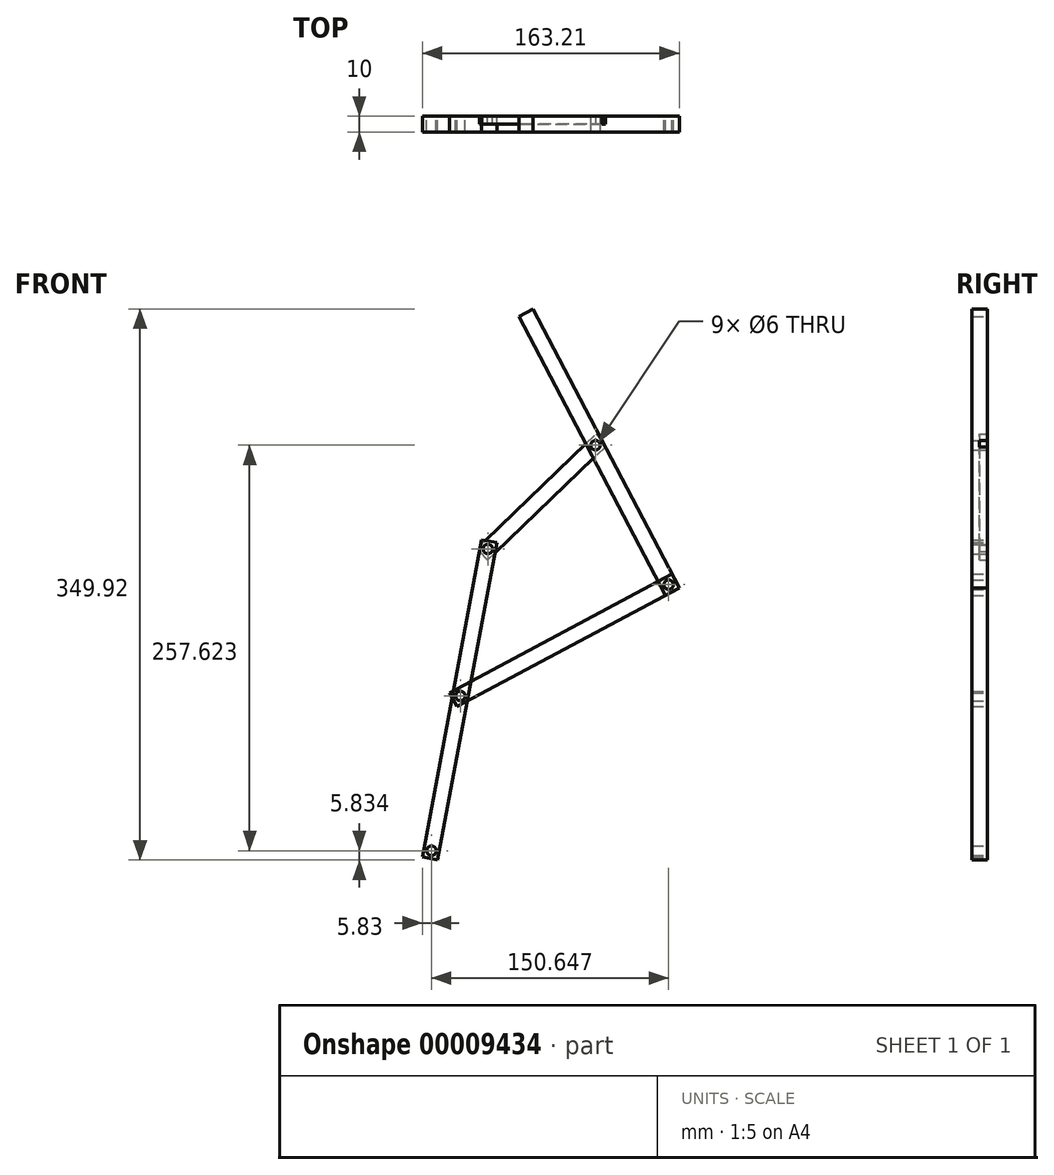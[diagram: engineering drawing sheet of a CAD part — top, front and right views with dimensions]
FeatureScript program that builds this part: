
annotation { "Feature Type Name" : "Feature", "Feature Type Description" : "" }
export const myFeature = defineFeature(function(context is Context, id is Id, definition is map)
    precondition{}
    {
        {
            var Q0;
            Q0=qCreatedBy(makeId("Front.planeOp"),FACE);
            var sketch = newSketch(context, id + "F0", { "sketchPlane" : qUnion([Q0])});
            skLineSegment(sketch, "E0", {"start": v(147.03, 163.63) * mm, "end": v(239.87, -13.52) * mm});
            skLineSegment(sketch, "E1", {"start": v(239.87, -13.52) * mm, "end": v(248.73, -8.87) * mm});
            skLineSegment(sketch, "E2", {"start": v(248.73, -8.87) * mm, "end": v(155.89, 168.27) * mm});
            skLineSegment(sketch, "E3", {"start": v(155.89, 168.27) * mm, "end": v(147.03, 163.63) * mm});
            skCircle(sketch, "E4", {"center": v(241.98, -6.77) * mm, "radius": 3 * mm});
            skCircle(sketch, "E5", {"center": v(195.56, 81.8) * mm, "radius": 3 * mm});
            skLineSegment(sketch, "E6", {"start": v(191.13, 79.49) * mm, "end": v(199.99, 84.13) * mm, "construction": true});
            skLineSegment(sketch, "E7", {"start": v(237.55, -9.09) * mm, "end": v(246.4, -4.45) * mm, "construction": true});
            skLineSegment(sketch, "E8", {"start": v(120.1, 15.99) * mm, "end": v(195.69, 88.88) * mm});
            skLineSegment(sketch, "E9", {"start": v(195.69, 88.88) * mm, "end": v(202.63, 81.68) * mm});
            skLineSegment(sketch, "E10", {"start": v(202.63, 81.68) * mm, "end": v(127.05, 8.8) * mm});
            skLineSegment(sketch, "E11", {"start": v(127.05, 8.8) * mm, "end": v(120.1, 15.99) * mm});
            skLineSegment(sketch, "E12", {"start": v(192.09, 85.4) * mm, "end": v(199.03, 78.2) * mm, "construction": true});
            skLineSegment(sketch, "E13", {"start": v(123.7, 19.46) * mm, "end": v(130.65, 12.26) * mm, "construction": true});
            skCircle(sketch, "E14", {"center": v(127.17, 15.86) * mm, "radius": 3 * mm});
            skLineSegment(sketch, "E15", {"start": v(102.94, -75.47) * mm, "end": v(244.03, 0) * mm});
            skLineSegment(sketch, "E16", {"start": v(244.03, 0) * mm, "end": v(248.74, -8.82) * mm});
            skLineSegment(sketch, "E17", {"start": v(248.74, -8.82) * mm, "end": v(107.66, -84.29) * mm});
            skLineSegment(sketch, "E18", {"start": v(107.66, -84.29) * mm, "end": v(102.94, -75.47) * mm});
            skLineSegment(sketch, "E19", {"start": v(239.62, -2.36) * mm, "end": v(244.34, -11.18) * mm, "construction": true});
            skLineSegment(sketch, "E20", {"start": v(107.35, -73.11) * mm, "end": v(112.07, -81.93) * mm, "construction": true});
            skCircle(sketch, "E21", {"center": v(109.71, -77.52) * mm, "radius": 3 * mm});
            skLineSegment(sketch, "E22", {"start": v(123.18, 21.7) * mm, "end": v(85.5, -179.81) * mm});
            skLineSegment(sketch, "E23", {"start": v(85.5, -179.81) * mm, "end": v(95.33, -181.65) * mm});
            skLineSegment(sketch, "E24", {"start": v(95.33, -181.65) * mm, "end": v(133, 19.86) * mm});
            skLineSegment(sketch, "E25", {"start": v(133, 19.86) * mm, "end": v(123.18, 21.7) * mm});
            skLineSegment(sketch, "E26", {"start": v(122.26, 16.78) * mm, "end": v(132.09, 14.94) * mm, "construction": true});
            skLineSegment(sketch, "E27", {"start": v(104.8, -76.6) * mm, "end": v(114.63, -78.44) * mm, "construction": true});
            skLineSegment(sketch, "E28", {"start": v(86.42, -174.9) * mm, "end": v(96.25, -176.74) * mm, "construction": true});
            skCircle(sketch, "E29", {"center": v(91.33, -175.82) * mm, "radius": 3 * mm});
            skSolve(sketch);
        }
        {
            var Q0;
            {var subQ7=sQuery(id+"F0.wireOp",EDGE,"E3");Q0=makeQuery(id+"F0.imprint","IMPRINT",FACE,{"disambiguationData":[TD([[makeQuery(id+"F0.imprint","IMPRINT",EDGE,{"derivedFrom":subQ7}),1.0]])]});}
            var Q1;
            Q1=makeQuery(id+"F0.imprint","IMPRINT",FACE,{"disambiguationData":[TD([[makeQuery(id+"F0.imprint","IMPRINT",EDGE,{"derivedFrom":sQuery(id+"F0.wireOp",EDGE,"E5")}),-1.0]])]});
            var Q2;
            {var subQ5=sQuery(id+"F0.wireOp",EDGE,"E0");var subQ7=sQuery(id+"F0.wireOp",EDGE,"E10");var subQ8=makeQuery(id+"F0.imprint","INTERSECT",VERTEX,{"derivedFrom":[subQ5,subQ7]});Q2=makeQuery(id+"F0.imprint","IMPRINT",FACE,{"disambiguationData":[TD([[makeQuery(id+"F0.imprint","IMPRINT",EDGE,{"disambiguationData":[TD([[subQ8,-1.0]])],"derivedFrom":subQ5}),1.0]])]});}
            var Q3;
            Q3=makeQuery(id+"F0.imprint","IMPRINT",FACE,{"disambiguationData":[TD([[makeQuery(id+"F0.imprint","IMPRINT",EDGE,{"derivedFrom":sQuery(id+"F0.wireOp",EDGE,"E4")}),-1.0]])]});
            extrude(context, id + "F1", {"entities" : qUnion([Q0, Q1, Q2, Q3]), "depth" : 10 * mm});
        }
        {
            var Q0;
            Q0=makeQuery(id+"F0.imprint","IMPRINT",FACE,{"disambiguationData":[TD([[makeQuery(id+"F0.imprint","IMPRINT",EDGE,{"derivedFrom":sQuery(id+"F0.wireOp",EDGE,"E5")}),-1.0]])]});
            var Q1;
            {var subQ1=sQuery(id+"F0.wireOp",EDGE,"E8");var subQ7=sQuery(id+"F0.wireOp",EDGE,"E0");var subQ9=makeQuery(id+"F0.imprint","INTERSECT",VERTEX,{"derivedFrom":[subQ7,subQ1]});Q1=makeQuery(id+"F0.imprint","IMPRINT",FACE,{"disambiguationData":[TD([[makeQuery(id+"F0.imprint","IMPRINT",EDGE,{"disambiguationData":[TD([[subQ9,-1.0]])],"derivedFrom":subQ7}),-1.0]])]});}
            var Q2;
            Q2=makeQuery(id+"F0.imprint","IMPRINT",FACE,{"disambiguationData":[TD([[makeQuery(id+"F0.imprint","IMPRINT",EDGE,{"derivedFrom":sQuery(id+"F0.wireOp",EDGE,"E14")}),-1.0]])]});
            extrude(context, id + "F2", {"entities" : qUnion([Q0, Q1, Q2]), "depth" : 5 * mm});
        }
        {
            var Q0;
            {var subQ3=sQuery(id+"F0.wireOp",EDGE,"E10");var subQ7=sQuery(id+"F0.wireOp",EDGE,"E11");var subQ9=makeQuery(id+"F0.imprint","INTERSECT",VERTEX,{"derivedFrom":[subQ3,subQ7]});Q0=makeQuery(id+"F0.imprint","IMPRINT",FACE,{"disambiguationData":[TD([[makeQuery(id+"F0.imprint","IMPRINT",EDGE,{"disambiguationData":[TD([[subQ9,1.0]])],"derivedFrom":subQ3}),1.0]])]});}
            var Q1;
            Q1=makeQuery(id+"F0.imprint","IMPRINT",FACE,{"disambiguationData":[TD([[makeQuery(id+"F0.imprint","IMPRINT",EDGE,{"derivedFrom":sQuery(id+"F0.wireOp",EDGE,"E14")}),-1.0]])]});
            var Q2;
            {var subQ1=sQuery(id+"F0.wireOp",EDGE,"E8");var subQ3=sQuery(id+"F0.wireOp",EDGE,"E22");var subQ5=makeQuery(id+"F0.imprint","INTERSECT",VERTEX,{"derivedFrom":[subQ1,subQ3]});Q2=makeQuery(id+"F0.imprint","IMPRINT",FACE,{"disambiguationData":[TD([[makeQuery(id+"F0.imprint","IMPRINT",EDGE,{"disambiguationData":[TD([[subQ5,-1.0]])],"derivedFrom":subQ1}),1.0]])]});}
            var Q3;
            Q3=makeQuery(id+"F0.imprint","IMPRINT",FACE,{"disambiguationData":[TD([[makeQuery(id+"F0.imprint","IMPRINT",EDGE,{"derivedFrom":sQuery(id+"F0.wireOp",EDGE,"E21")}),-1.0]])]});
            var Q4;
            {var subQ0=sQuery(id+"F0.wireOp",EDGE,"E23");var subQ1=sQuery(id+"F0.wireOp",EDGE,"E18");var subQ2=makeQuery(id+"F0.imprint","INTERSECT",VERTEX,{"derivedFrom":[subQ1,subQ0]});Q4=makeQuery(id+"F0.imprint","IMPRINT",FACE,{"disambiguationData":[TD([[makeQuery(id+"F0.imprint","IMPRINT",EDGE,{"disambiguationData":[TD([[subQ2,-1.0]])],"derivedFrom":subQ1}),1.0]])]});}
            var Q5;
            {var subQ0=sQuery(id+"F0.wireOp",EDGE,"E24");var subQ1=sQuery(id+"F0.wireOp",EDGE,"E17");var subQ2=makeQuery(id+"F0.imprint","INTERSECT",VERTEX,{"derivedFrom":[subQ1,subQ0]});Q5=makeQuery(id+"F0.imprint","IMPRINT",FACE,{"disambiguationData":[TD([[makeQuery(id+"F0.imprint","IMPRINT",EDGE,{"disambiguationData":[TD([[subQ2,-1.0]])],"derivedFrom":subQ1}),1.0]])]});}
            extrude(context, id + "F3", {"entities" : qUnion([Q0, Q1, Q2, Q3, Q4, Q5]), "depth" : 10 * mm});
        }
        {
            var Q0;
            {var subQ5=sQuery(id+"F0.wireOp",EDGE,"E1");var subQ7=sQuery(id+"F0.wireOp",EDGE,"E0");var subQ9=makeQuery(id+"F0.imprint","INTERSECT",VERTEX,{"derivedFrom":[subQ7,subQ5]});Q0=makeQuery(id+"F0.imprint","IMPRINT",FACE,{"disambiguationData":[TD([[makeQuery(id+"F0.imprint","IMPRINT",EDGE,{"disambiguationData":[TD([[subQ9,1.0]])],"derivedFrom":subQ7}),-1.0]])]});}
            var Q1;
            Q1=makeQuery(id+"F0.imprint","IMPRINT",FACE,{"disambiguationData":[TD([[makeQuery(id+"F0.imprint","IMPRINT",EDGE,{"derivedFrom":sQuery(id+"F0.wireOp",EDGE,"E4")}),-1.0]])]});
            var Q2;
            Q2=makeQuery(id+"F0.imprint","IMPRINT",FACE,{"disambiguationData":[TD([[makeQuery(id+"F0.imprint","IMPRINT",EDGE,{"derivedFrom":sQuery(id+"F0.wireOp",EDGE,"E21")}),-1.0]])]});
            var Q3;
            {var subQ1=sQuery(id+"F0.wireOp",EDGE,"E18");var subQ3=sQuery(id+"F0.wireOp",EDGE,"E15");var subQ5=makeQuery(id+"F0.imprint","INTERSECT",VERTEX,{"derivedFrom":[subQ3,subQ1]});Q3=makeQuery(id+"F0.imprint","IMPRINT",FACE,{"disambiguationData":[TD([[makeQuery(id+"F0.imprint","IMPRINT",EDGE,{"disambiguationData":[TD([[subQ5,-1.0]])],"derivedFrom":subQ3}),-1.0]])]});}
            var Q4;
            {var subQ1=sQuery(id+"F0.wireOp",EDGE,"E18");var subQ3=sQuery(id+"F0.wireOp",EDGE,"E17");var subQ5=makeQuery(id+"F0.imprint","INTERSECT",VERTEX,{"derivedFrom":[subQ3,subQ1]});Q4=makeQuery(id+"F0.imprint","IMPRINT",FACE,{"disambiguationData":[TD([[makeQuery(id+"F0.imprint","IMPRINT",EDGE,{"disambiguationData":[TD([[subQ5,1.0]])],"derivedFrom":subQ3}),-1.0]])]});}
            extrude(context, id + "F4", {"entities" : qUnion([Q0, Q1, Q2, Q3, Q4]), "depth" : 10 * mm});
        }
    });
